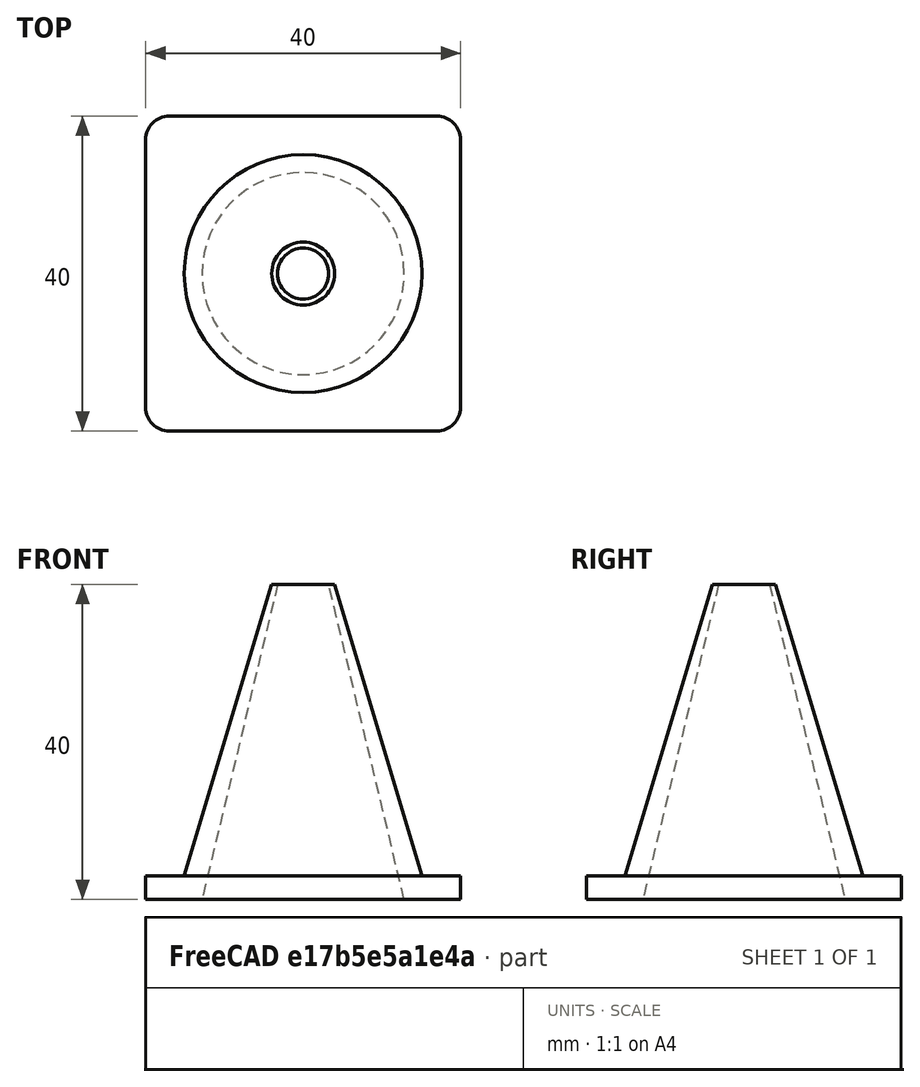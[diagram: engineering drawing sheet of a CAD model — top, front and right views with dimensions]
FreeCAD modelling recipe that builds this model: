
FCSTD DOCUMENT  (FreeCAD 1.0R39319 (Git))
Label: ojt1_t14r02_con
License: All rights reserved
LicenseURL: https://en.wikipedia.org/wiki/All_rights_reserved
objects: Part::Cone×2, Part::Box×1, Part::Fillet×1, Part::MultiFuse×1, Part::Cut×1
note: 6 computed .brp shape members not serialized (recipe doc carries the construction recipe); baked Part::Feature solids carry a one-line shape summary decoded from their .brp

FEATURE [Part::Cone] Cone  label="Con"
  Angle = 360
  AttacherType = Attacher::AttachEngine3D
  Height = 40
  Radius1 = 16
  Radius2 = 4
FEATURE [Part::Box] Box  label="Cub"
  AttacherType = Attacher::AttachEngine3D
  Height = 3
  Length = 40
  Placement = pos=(-20,-20,0) rot=(0,0,1;0rad)
  Width = 40
FEATURE [Part::Fillet] Fillet
  Base = -> Box
  EdgeLinks = -> Box [Edge1,Edge3,Edge5,Edge7]
  Edges = 4 edges r=3: [Edge1,Edge3,Edge5,Edge7]
FEATURE [Part::Cone] Cone001  label="Con001"
  Angle = 360
  AttacherType = Attacher::AttachEngine3D
  Height = 50
  Placement = pos=(0,0,-9) rot=(0,0,1;0rad)
  Radius1 = 15
  Radius2 = 3
FEATURE [Part::MultiFuse] Fusion
  Shapes = -> [Cone,Fillet]
FEATURE [Part::Cut] Cut
  Base = -> Fusion
  Placement = pos=(20,20,0) rot=(0,0,1;0rad)
  Tool = -> Cone001
